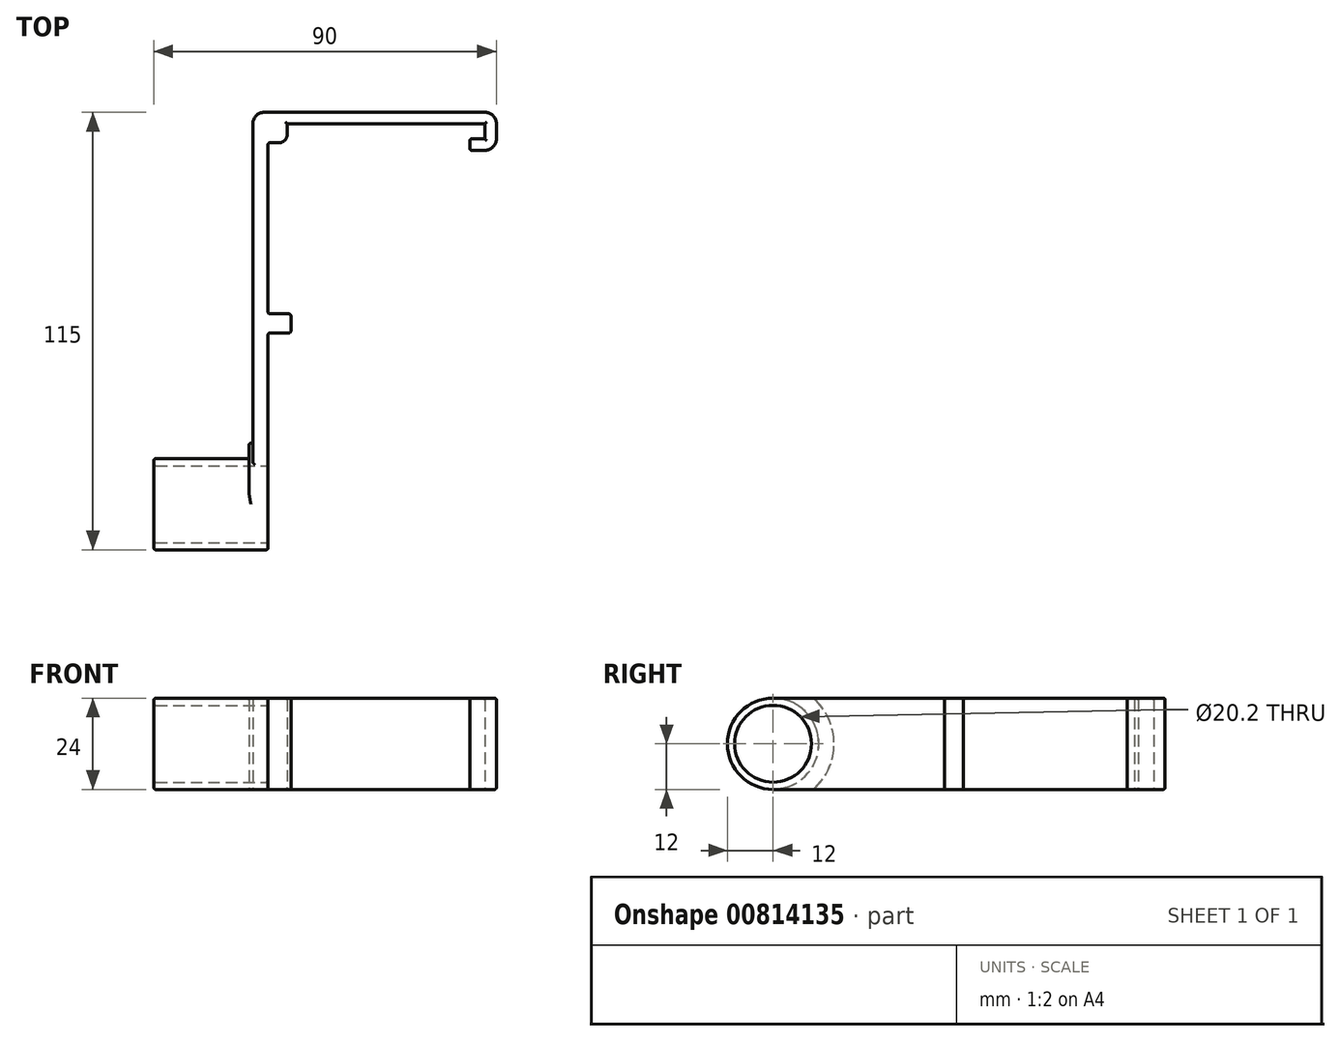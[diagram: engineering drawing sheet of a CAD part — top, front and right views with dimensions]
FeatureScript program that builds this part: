
annotation { "Feature Type Name" : "Feature", "Feature Type Description" : "" }
export const myFeature = defineFeature(function(context is Context, id is Id, definition is map)
    precondition{}
    {
        {
            var Q0;
            Q0=qCreatedBy(makeId("Top.planeOp"),FACE);
            var sketch = newSketch(context, id + "F0", { "sketchPlane" : qUnion([Q0])});
            skLineSegment(sketch, "E0", {"start": v(0, 0) * mm, "end": v(0, 130) * mm});
            skLineSegment(sketch, "E1", {"start": v(0, 130) * mm, "end": v(64, 130) * mm});
            skLineSegment(sketch, "E2", {"start": v(64, 130) * mm, "end": v(64, 120) * mm});
            skLineSegment(sketch, "E3", {"start": v(64, 120) * mm, "end": v(57, 120) * mm});
            skLineSegment(sketch, "E4", {"start": v(57, 120) * mm, "end": v(57, 123) * mm});
            skLineSegment(sketch, "E5", {"start": v(57, 123) * mm, "end": v(61, 123) * mm});
            skLineSegment(sketch, "E6", {"start": v(61, 123) * mm, "end": v(61, 127) * mm});
            skLineSegment(sketch, "E7", {"start": v(61, 127) * mm, "end": v(9, 127) * mm});
            skLineSegment(sketch, "E8", {"start": v(4, 0) * mm, "end": v(0, 0) * mm});
            skLineSegment(sketch, "E9.trimOffspring", {"start": v(4, 122) * mm, "end": v(4, 77) * mm});
            skLineSegment(sketch, "E10", {"start": v(4, 77) * mm, "end": v(10, 77) * mm});
            skLineSegment(sketch, "E11", {"start": v(10, 77) * mm, "end": v(10, 72) * mm});
            skLineSegment(sketch, "E12", {"start": v(10, 72) * mm, "end": v(4, 72) * mm});
            skLineSegment(sketch, "E13.trimOffspring", {"start": v(4, 72) * mm, "end": v(4, 0) * mm});
            skLineSegment(sketch, "E14", {"start": v(9, 127) * mm, "end": v(9, 122) * mm});
            skLineSegment(sketch, "E15", {"start": v(9, 122) * mm, "end": v(4, 122) * mm});
            skSolve(sketch);
        }
        {
            var Q0;
            Q0 = qSketchRegion(id + "F0", true);
            extrude(context, id + "F1", {"entities" : qUnion([Q0]), "depth" : 24 * mm, "offsetDistance" : 25 * mm, "symmetric" : true});
        }
        {
            var Q0;
            Q0=makeQuery(id+"F1.opExtrude","SWEPT_FACE",FACE,{"disambiguationData":[OSD([sQuery(id+"F0.wireOp",EDGE,"E9.trimOffspring")])]});
            var sketch = newSketch(context, id + "F2", { "sketchPlane" : qUnion([Q0])});
            skCircle(sketch, "E16", {"center": v(27, 0) * mm, "radius": 12 * mm});
            skCircle(sketch, "E17", {"center": v(27, 0) * mm, "radius": 10.1 * mm});
            skSolve(sketch);
        }
        {
            var Q0;
            Q0 = qSketchRegion(id + "F2", true);
            extrude(context, id + "F3", {"entities" : qUnion([Q0]), "operationType" : NewBodyOperationType.ADD, "oppositeDirection" : true, "depth" : 30 * mm, "offsetDistance" : 25 * mm});
        }
        {
            var Q0;
            Q0=makeQuery(id+"F2.imprint","IMPRINT",FACE,{"disambiguationData":[TD([[makeQuery(id+"F2.imprint","IMPRINT",EDGE,{"derivedFrom":sQuery(id+"F2.wireOp",EDGE,"E17")}),1.0]])]});
            extrude(context, id + "F4", {"entities" : qUnion([Q0]), "operationType" : NewBodyOperationType.REMOVE, "endBound" : BoundingType.UP_TO_NEXT, "oppositeDirection" : true, "depth" : 25 * mm, "offsetDistance" : 25 * mm});
        }
        {
            var Q0;
            {var subQ1=sQuery(id+"F0.wireOp",EDGE,"E9.trimOffspring");var subQ6=makeQuery(id+"F1.opExtrude","SWEPT_EDGE",EDGE,{"disambiguationData":[OSD([sQuery(id+"F0.wireOp",EDGE,"E8"),subQ1])]});Q0=makeQuery(id+"F2.imprint","IMPRINT",FACE,{"disambiguationData":[TD([[makeQuery(id+"F2.imprint","IMPRINT",EDGE,{"derivedFrom":subQ6}),1.0]])]});}
            var sketch = newSketch(context, id + "F5", { "sketchPlane" : qUnion([Q0])});
            skArc(sketch, "E18", {"start": v(27, 12) * mm, "mid": v(15, -0.01) * mm, "end": v(27.03, -12) * mm});
            skLineSegment(sketch, "E19", {"start": v(27, 12) * mm, "end": v(0, 12) * mm});
            skLineSegment(sketch, "E20", {"start": v(0, 12) * mm, "end": v(0, -12.06) * mm});
            skLineSegment(sketch, "E21", {"start": v(0, -12.06) * mm, "end": v(27.03, -12) * mm});
            skSolve(sketch);
        }
        {
            var Q0;
            Q0 = qSketchRegion(id + "F5", true);
            var Q1;
            {var subQ3=sQuery(id+"F0.wireOp",EDGE,"E8");var subQ12=sQuery(id+"F0.wireOp",EDGE,"E0");var subQ13=makeQuery(id+"F1.opExtrude","SWEPT_FACE",FACE,{"disambiguationData":[OSD([subQ12])]});Q1=makeQuery(id+"F3.boolean.opBoolean","SPLIT",FACE,{"disambiguationData":[TD([makeQuery(id+"F1.opExtrude","SWEPT_FACE",FACE,{"disambiguationData":[OSD([subQ3])]})])],"derivedFrom":subQ13});}
            extrude(context, id + "F6", {"entities" : qUnion([Q0]), "operationType" : NewBodyOperationType.REMOVE, "endBound" : BoundingType.UP_TO_SURFACE, "oppositeDirection" : true, "depth" : 32.3 * mm, "endBoundEntityFace" : qUnion([Q1]), "offsetDistance" : 25 * mm});
        }
        {
            var Q0;
            Q0=makeQuery(id+"F1.opExtrude","SWEPT_EDGE",EDGE,{"disambiguationData":[OSD([sQuery(id+"F0.wireOp",EDGE,"E0"),sQuery(id+"F0.wireOp",EDGE,"E1")])]});
            var Q1;
            Q1=makeQuery(id+"F1.opExtrude","SWEPT_EDGE",EDGE,{"disambiguationData":[OSD([sQuery(id+"F0.wireOp",EDGE,"E2"),sQuery(id+"F0.wireOp",EDGE,"E3")])]});
            var Q2;
            Q2=makeQuery(id+"F1.opExtrude","SWEPT_EDGE",EDGE,{"disambiguationData":[OSD([sQuery(id+"F0.wireOp",EDGE,"E1"),sQuery(id+"F0.wireOp",EDGE,"E2")])]});
            fillet(context, id + "F7", {"entities" : qUnion([Q0, Q1, Q2]), "radius" : 3 * mm, "tangentPropagation" : true, "allowEdgeOverflow" : false});
        }
        {
            var Q0;
            {var subQ0=sQuery(id+"F0.wireOp",EDGE,"E1");var subQ15=sQuery(id+"F0.wireOp",EDGE,"E0");var subQ16=makeQuery(id+"F1.opExtrude","SWEPT_FACE",FACE,{"disambiguationData":[OSD([subQ15])]});Q0=makeQuery(id+"F3.boolean.opBoolean","SPLIT",FACE,{"disambiguationData":[TD([makeQuery(id+"F1.opExtrude","SWEPT_FACE",FACE,{"disambiguationData":[OSD([subQ0])]})])],"derivedFrom":subQ16});}
            var sketch = newSketch(context, id + "F8", { "sketchPlane" : qUnion([Q0])});
            skArc(sketch, "E22", {"start": v(-27, 12) * mm, "mid": v(-39, 0) * mm, "end": v(-27, -12) * mm});
            skArc(sketch, "E23", {"start": v(-37.58, 12) * mm, "mid": v(-43, 0) * mm, "end": v(-37.58, -12) * mm});
            skLineSegment(sketch, "E24", {"start": v(-27, -12) * mm, "end": v(-37.58, -12) * mm});
            skLineSegment(sketch, "E25", {"start": v(-27, 12) * mm, "end": v(-37.58, 12) * mm});
            skSolve(sketch);
        }
        {
            var Q0;
            Q0 = qSketchRegion(id + "F8", true);
            extrude(context, id + "F9", {"entities" : qUnion([Q0]), "operationType" : NewBodyOperationType.ADD, "depth" : 1 * mm, "offsetDistance" : 25 * mm});
        }
        {
            var Q0;
            Q0=makeQuery(id+"F1.opExtrude","SWEPT_FACE",FACE,{"disambiguationData":[OSD([sQuery(id+"F0.wireOp",EDGE,"E13.trimOffspring")])]});
            var Q1;
            Q1=makeQuery(id+"F1.opExtrude","SWEPT_FACE",FACE,{"disambiguationData":[OSD([sQuery(id+"F0.wireOp",EDGE,"E11")])]});
            var Q2;
            Q2=makeQuery(id+"F1.opExtrude","SWEPT_FACE",FACE,{"disambiguationData":[OSD([sQuery(id+"F0.wireOp",EDGE,"E9.trimOffspring")])]});
            var Q3;
            Q3=makeQuery(id+"F1.opExtrude","SWEPT_FACE",FACE,{"disambiguationData":[OSD([sQuery(id+"F0.wireOp",EDGE,"E4")])]});
            var Q4;
            Q4=makeQuery(id+"F9.boolean.opBoolean","MERGE",FACE,{"derivedFrom":[makeQuery(id+"F1.opExtrude","CAP_FACE",FACE,{"disambiguationData":[OSD([sQuery(id+"F0.wireOp",EDGE,"E0"),sQuery(id+"F0.wireOp",EDGE,"E1"),sQuery(id+"F0.wireOp",EDGE,"E2"),sQuery(id+"F0.wireOp",EDGE,"E3"),sQuery(id+"F0.wireOp",EDGE,"E4"),sQuery(id+"F0.wireOp",EDGE,"E5"),sQuery(id+"F0.wireOp",EDGE,"E6"),sQuery(id+"F0.wireOp",EDGE,"E7"),sQuery(id+"F0.wireOp",EDGE,"E8"),sQuery(id+"F0.wireOp",EDGE,"E9.trimOffspring"),sQuery(id+"F0.wireOp",EDGE,"E10"),sQuery(id+"F0.wireOp",EDGE,"E11"),sQuery(id+"F0.wireOp",EDGE,"E12"),sQuery(id+"F0.wireOp",EDGE,"E13.trimOffspring")])],"isStart":true}),makeQuery(id+"F9.opExtrude","SWEPT_FACE",FACE,{"disambiguationData":[OSD([sQuery(id+"F8.wireOp",EDGE,"E24")])]})]});
            var Q5;
            Q5=makeQuery(id+"F9.boolean.opBoolean","MERGE",FACE,{"derivedFrom":[makeQuery(id+"F1.opExtrude","CAP_FACE",FACE,{"disambiguationData":[OSD([sQuery(id+"F0.wireOp",EDGE,"E0"),sQuery(id+"F0.wireOp",EDGE,"E1"),sQuery(id+"F0.wireOp",EDGE,"E2"),sQuery(id+"F0.wireOp",EDGE,"E3"),sQuery(id+"F0.wireOp",EDGE,"E4"),sQuery(id+"F0.wireOp",EDGE,"E5"),sQuery(id+"F0.wireOp",EDGE,"E6"),sQuery(id+"F0.wireOp",EDGE,"E7"),sQuery(id+"F0.wireOp",EDGE,"E8"),sQuery(id+"F0.wireOp",EDGE,"E9.trimOffspring"),sQuery(id+"F0.wireOp",EDGE,"E10"),sQuery(id+"F0.wireOp",EDGE,"E11"),sQuery(id+"F0.wireOp",EDGE,"E12"),sQuery(id+"F0.wireOp",EDGE,"E13.trimOffspring")])],"isStart":false}),makeQuery(id+"F9.opExtrude","SWEPT_FACE",FACE,{"disambiguationData":[OSD([sQuery(id+"F8.wireOp",EDGE,"E25")])]})]});
            var Q6;
            Q6=makeQuery(id+"F3.opExtrude","CAP_FACE",FACE,{"disambiguationData":[OSD([sQuery(id+"F2.wireOp",EDGE,"E16"),sQuery(id+"F2.wireOp",EDGE,"E17")])],"isStart":false});
            var Q7;
            Q7=makeQuery(id+"F9.opExtrude","CAP_EDGE",EDGE,{"disambiguationData":[OSD([sQuery(id+"F8.wireOp",EDGE,"E23")])],"isStart":false});
            var Q8;
            Q8=makeQuery(id+"F9.opExtrude","CAP_EDGE",EDGE,{"disambiguationData":[OSD([sQuery(id+"F8.wireOp",EDGE,"E23")])],"isStart":true});
            fillet(context, id + "F10", {"entities" : qUnion([Q0, Q1, Q2, Q3, Q4, Q5, Q6, Q7, Q8]), "radius" : .5 * mm, "tangentPropagation" : true, "defaultsChanged" : false, "vertexSettings" : [], "allowEdgeOverflow" : false});
        }
        {
            var Q0;
            Q0=makeQuery(id+"F1.opExtrude","SWEPT_EDGE",EDGE,{"disambiguationData":[OSD([sQuery(id+"F0.wireOp",EDGE,"E14"),sQuery(id+"F0.wireOp",EDGE,"E15")])]});
            fillet(context, id + "F11", {"entities" : qUnion([Q0]), "radius" : 2 * mm, "tangentPropagation" : true, "allowEdgeOverflow" : false});
        }
    });
